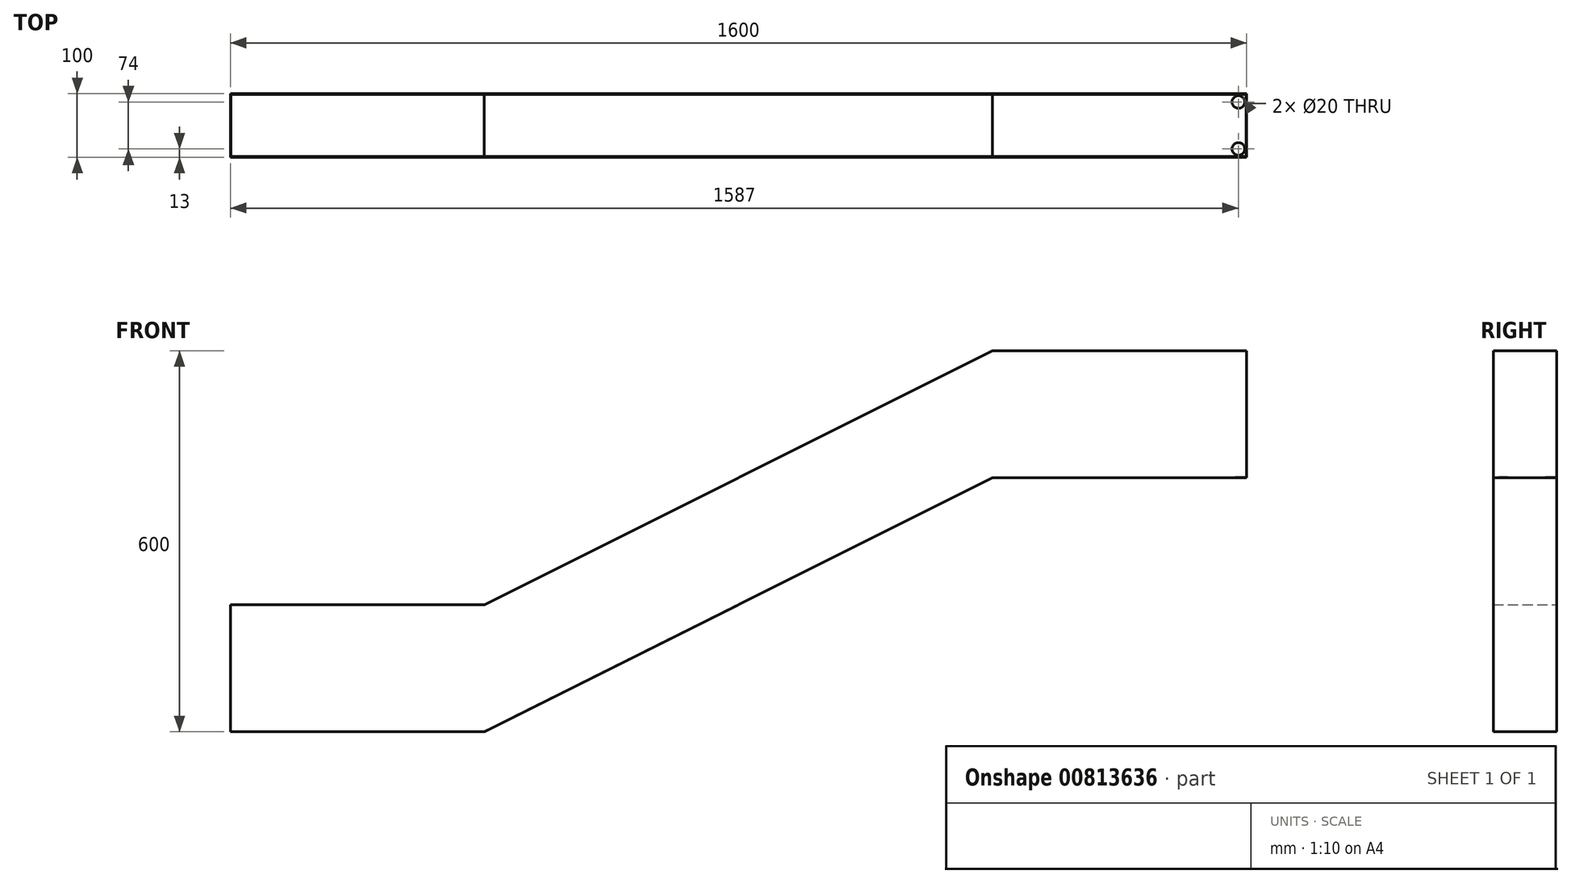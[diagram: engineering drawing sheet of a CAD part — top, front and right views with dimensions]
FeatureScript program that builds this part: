
annotation { "Feature Type Name" : "Feature", "Feature Type Description" : "" }
export const myFeature = defineFeature(function(context is Context, id is Id, definition is map)
    precondition{}
    {
        {
            var Q0;
            Q0=qCreatedBy(makeId("Front.planeOp"),FACE);
            var sketch = newSketch(context, id + "F0", { "sketchPlane" : qUnion([Q0])});
            skLineSegment(sketch, "E0", {"start": v(0, 0) * mm, "end": v(400, 0) * mm});
            skLineSegment(sketch, "E1", {"start": v(400, 0) * mm, "end": v(1200, 400) * mm});
            skLineSegment(sketch, "E2", {"start": v(1200, 400) * mm, "end": v(1600, 400) * mm});
            skLineSegment(sketch, "E3.0", {"start": v(1200, 600) * mm, "end": v(1600, 600) * mm});
            skLineSegment(sketch, "E4.0", {"start": v(0, 200) * mm, "end": v(400, 200) * mm});
            skLineSegment(sketch, "E5", {"start": v(400, 200) * mm, "end": v(1200, 600) * mm});
            skLineSegment(sketch, "E6", {"start": v(1600, 600) * mm, "end": v(1600, 400) * mm});
            skLineSegment(sketch, "E7", {"start": v(0, 200) * mm, "end": v(0, 0) * mm});
            skSolve(sketch);
        }
        {
            var Q0;
            Q0=makeQuery(id+"F0.imprint","IMPRINT",FACE,{"disambiguationData":[TD([[makeQuery(id+"F0.imprint","IMPRINT",EDGE,{"derivedFrom":sQuery(id+"F0.wireOp",EDGE,"E0")}),1.0]])]});
            extrude(context, id + "F1", {"entities" : qUnion([Q0]), "depth" : 100 * mm, "offsetDistance" : 25 * mm});
        }
        {
            var Q0;
            Q0=makeQuery(id+"F1.opExtrude","SWEPT_FACE",FACE,{"disambiguationData":[OSD([sQuery(id+"F0.wireOp",EDGE,"E4.0")])]});
            var Q1;
            Q1=makeQuery(id+"F1.opExtrude","SWEPT_FACE",FACE,{"disambiguationData":[OSD([sQuery(id+"F0.wireOp",EDGE,"E5")])]});
            var Q2;
            Q2=makeQuery(id+"F1.opExtrude","SWEPT_FACE",FACE,{"disambiguationData":[OSD([sQuery(id+"F0.wireOp",EDGE,"E3.0")])]});
            shell(context, id + "F2", {"entities" : qUnion([Q0, Q1, Q2]), "thickness" : 1 * mm});
        }
        {
            var Q0;
            Q0=makeQuery(id+"F2.opShell","OFFSET_FACE",FACE,{"disambiguationData":[OSD([sQuery(id+"F0.wireOp",EDGE,"E2")])]});
            var sketch = newSketch(context, id + "F3", { "sketchPlane" : qUnion([Q0])});
            skCircle(sketch, "E8", {"center": v(1587, -13) * mm, "radius": 12 * mm});
            skCircle(sketch, "E9.0", {"center": v(1587, -13) * mm, "radius": 10 * mm});
            skCircle(sketch, "E10", {"center": v(1587, -87) * mm, "radius": 12 * mm});
            skCircle(sketch, "E11.0", {"center": v(1587, -87) * mm, "radius": 10 * mm});
            skSolve(sketch);
        }
        {
            var Q0;
            Q0=sQuery(id+"F3.wireOp",EDGE,"E9.0");
            var Q1;
            Q1=sQuery(id+"F3.wireOp",EDGE,"E8");
            var Q2;
            Q2=sQuery(id+"F3.wireOp",EDGE,"E11.0");
            var Q3;
            Q3=sQuery(id+"F3.wireOp",EDGE,"E10");
            extrude(context, id + "F4", {"bodyType" : ToolBodyType.SURFACE, "surfaceEntities" : qUnion([Q0, Q1, Q2, Q3]), "depth" : 200 * mm, "offsetDistance" : 25 * mm});
        }
        {
            var Q0;
            Q0=sQuery(id+"F3.wireOp",VERTEX,"E8.center");
            var Q1;
            Q1=sQuery(id+"F3.wireOp",VERTEX,"E11.0.center");
            var Q2;
            Q2=makeQuery(id+"F1.opExtrude","SWEPT_BODY",BODY,{"disambiguationData":[OSD([sQuery(id+"F0.wireOp",EDGE,"E0"),sQuery(id+"F0.wireOp",EDGE,"E1"),sQuery(id+"F0.wireOp",EDGE,"E2"),sQuery(id+"F0.wireOp",EDGE,"E3.0"),sQuery(id+"F0.wireOp",EDGE,"E4.0"),sQuery(id+"F0.wireOp",EDGE,"E5"),sQuery(id+"F0.wireOp",EDGE,"E6"),sQuery(id+"F0.wireOp",EDGE,"E7")])]});
            hole(context, id + "F5", {"style" : HoleStyle.SIMPLE, "endStyle" : HoleEndStyle.THROUGH, "holeDiameter" : 20 * mm, "majorDiameter" : 5 * mm, "isTappedThrough" : true, "tappedDepth" : 12 * mm, "tapClearance" : 3, "locations" : qUnion([Q0, Q1]), "scope" : qUnion([Q2])});
        }
        {
            var Q0;
            Q0=makeQuery(id+"F1.opExtrude","SWEPT_FACE",FACE,{"disambiguationData":[OSD([sQuery(id+"F0.wireOp",EDGE,"E0")])]});
            var sketch = newSketch(context, id + "F6", { "sketchPlane" : qUnion([Q0])});
            skCircle(sketch, "E12", {"center": v(12, 88) * mm, "radius": 12 * mm});
            skCircle(sketch, "E13", {"center": v(12, 12) * mm, "radius": 12 * mm});
            skCircle(sketch, "E14.0", {"center": v(12, 12) * mm, "radius": 10 * mm});
            skCircle(sketch, "E15.0", {"center": v(12, 88) * mm, "radius": 10 * mm});
            skSolve(sketch);
        }
        {
            var Q0;
            Q0=sQuery(id+"F6.wireOp",EDGE,"E15.0");
            var Q1;
            Q1=sQuery(id+"F6.wireOp",EDGE,"E12");
            var Q2;
            Q2=sQuery(id+"F6.wireOp",EDGE,"E14.0");
            var Q3;
            Q3=sQuery(id+"F6.wireOp",EDGE,"E13");
            extrude(context, id + "F7", {"bodyType" : ToolBodyType.SURFACE, "surfaceEntities" : qUnion([Q0, Q1, Q2, Q3]), "oppositeDirection" : true, "depth" : 200 * mm, "offsetDistance" : 25 * mm});
        }
    });
